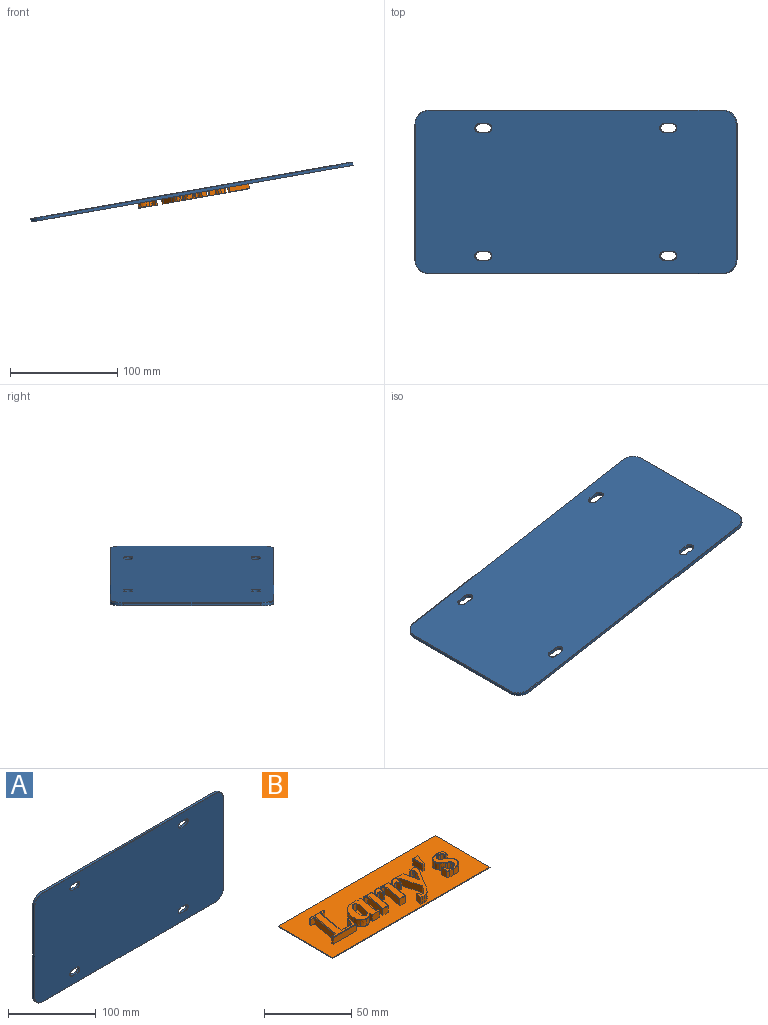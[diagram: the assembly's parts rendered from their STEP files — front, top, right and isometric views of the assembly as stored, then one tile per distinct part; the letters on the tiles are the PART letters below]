
ASSEMBLY  parts=2 mates=2
PART A: 50 faces, bbox 306.9x3.2x154.5 mm
  f0: cylinder r=12.7mm len=12.7mm, axis (0,1,0), area 55.7mm2, adj f1,f7,f9,f46
  f1: plane 279.4x2.79mm, normal (0,0,1), area 780.6mm2, adj f0,f2,f9,f44
  f2: cylinder r=12.7mm len=12.7mm, axis (0,1,0), area 55.7mm2, adj f1,f3,f9,f42
  f3: plane 127x2.79mm, normal (-1,0,0), area 354.8mm2, adj f2,f4,f9,f43
  f4: cylinder r=12.7mm len=12.7mm, axis (0,1,0), area 55.7mm2, adj f3,f5,f9,f45
  f5: plane 279.4x2.79mm, normal (0,0,-1), area 780.6mm2, adj f4,f6,f9,f47
  f6: cylinder r=12.7mm len=12.7mm, axis (0,1,0), area 55.7mm2, adj f5,f7,f9,f49
  f7: plane 127x2.79mm, normal (1,0,0), area 354.8mm2, adj f0,f6,f9,f48
  f8: plane 304.04x151.64mm, normal (0,-1,0), area 45497.2mm2, adj f26,f27,f28,f29,f30,f31,f32,f33
  f9: plane 304.8x152.4mm, normal (0,1,0), area 45898.4mm2, adj f0,f1,f2,f3,f4,f5,f6,f7
  f10: plane 7.62x2.79mm, normal (0,0,1), area 21.3mm2, adj f9,f11,f13,f39
  f11: cylinder r=3.81mm len=7.62mm, axis (0,-1,0), area 33.4mm2, adj f9,f10,f12,f41
  f12: plane 7.62x2.79mm, normal (0,0,-1), area 21.3mm2, adj f9,f11,f13,f40
  f13: cylinder r=3.81mm len=7.62mm, axis (0,-1,0), area 33.4mm2, adj f9,f10,f12,f38
  f14: cylinder r=3.81mm len=7.62mm, axis (0,-1,0), area 33.4mm2, adj f9,f15,f17,f34
  f15: plane 7.62x2.79mm, normal (0,0,1), area 21.3mm2, adj f9,f14,f16,f35
  f16: cylinder r=3.81mm len=7.62mm, axis (0,-1,0), area 33.4mm2, adj f9,f15,f17,f37
  f17: plane 7.62x2.79mm, normal (0,0,-1), area 21.3mm2, adj f9,f14,f16,f36
  f18: cylinder r=3.81mm len=7.62mm, axis (0,-1,0), area 33.4mm2, adj f9,f19,f21,f31
  f19: plane 7.62x2.79mm, normal (0,0,1), area 21.3mm2, adj f9,f18,f20,f33
  f20: cylinder r=3.81mm len=7.62mm, axis (0,-1,0), area 33.4mm2, adj f9,f19,f21,f32
  f21: plane 7.62x2.79mm, normal (0,0,-1), area 21.3mm2, adj f9,f18,f20,f30
  f22: cylinder r=3.81mm len=7.62mm, axis (0,-1,0), area 33.4mm2, adj f9,f23,f25,f27
  f23: plane 7.62x2.79mm, normal (0,0,1), area 21.3mm2, adj f9,f22,f24,f29
  f24: cylinder r=3.81mm len=7.62mm, axis (0,-1,0), area 33.4mm2, adj f9,f23,f25,f28
  f25: plane 7.62x2.79mm, normal (0,0,-1), area 21.3mm2, adj f9,f22,f24,f26
  f26: cylinder r=0.38mm len=7.62mm, axis (1,0,0), area 4.6mm2, adj f8,f25,f27,f28
  f27: torus R=4.19mm, axis (0,-1,0), area 7.4mm2, adj f8,f22,f26,f29
  f28: torus R=4.19mm, axis (0,-1,0), area 7.4mm2, adj f8,f24,f26,f29
  f29: cylinder r=0.38mm len=7.62mm, axis (-1,0,0), area 4.6mm2, adj f8,f23,f27,f28
  f30: cylinder r=0.38mm len=7.62mm, axis (1,0,0), area 4.6mm2, adj f8,f21,f31,f32
  f31: torus R=4.19mm, axis (0,-1,0), area 7.4mm2, adj f8,f18,f30,f33
  f32: torus R=4.19mm, axis (0,-1,0), area 7.4mm2, adj f8,f20,f30,f33
  f33: cylinder r=0.38mm len=7.62mm, axis (-1,0,0), area 4.6mm2, adj f8,f19,f31,f32
  f34: torus R=4.19mm, axis (0,-1,0), area 7.4mm2, adj f8,f14,f35,f36
  f35: cylinder r=0.38mm len=7.62mm, axis (-1,0,0), area 4.6mm2, adj f8,f15,f34,f37
  f36: cylinder r=0.38mm len=7.62mm, axis (1,0,0), area 4.6mm2, adj f8,f17,f34,f37
  f37: torus R=4.19mm, axis (0,-1,0), area 7.4mm2, adj f8,f16,f35,f36
  f38: torus R=4.19mm, axis (0,-1,0), area 7.4mm2, adj f8,f13,f39,f40
  f39: cylinder r=0.38mm len=7.62mm, axis (-1,0,0), area 4.6mm2, adj f8,f10,f38,f41
  f40: cylinder r=0.38mm len=7.62mm, axis (1,0,0), area 4.6mm2, adj f8,f12,f38,f41
  f41: torus R=4.19mm, axis (0,-1,0), area 7.4mm2, adj f8,f11,f39,f40
  f42: torus R=12.32mm, axis (0,-1,0), area 11.8mm2, adj f2,f8,f43,f44
  f43: cylinder r=0.38mm len=127mm, axis (0,0,1), area 76mm2, adj f3,f8,f42,f45
  f44: cylinder r=0.38mm len=279.4mm, axis (1,0,0), area 167.2mm2, adj f1,f8,f42,f46
  f45: torus R=12.32mm, axis (0,-1,0), area 11.8mm2, adj f4,f8,f43,f47
  f46: torus R=12.32mm, axis (0,-1,0), area 11.8mm2, adj f0,f8,f44,f48
  f47: cylinder r=0.38mm len=279.4mm, axis (-1,0,0), area 167.2mm2, adj f5,f8,f45,f49
  f48: cylinder r=0.38mm len=127mm, axis (0,0,-1), area 76mm2, adj f7,f8,f46,f49
  f49: torus R=12.32mm, axis (0,-1,0), area 11.8mm2, adj f6,f8,f47,f48
PART B: 223 faces, bbox 127x44.5x5.3 mm
  f0: plane 127x44.45mm, normal (0,0,1), area 4801.8mm2, adj f1,f2,f3,f4,f6,f7,f8,f9
  f1: plane 127x0.51mm, normal (0,-1,0), area 64.5mm2, adj f0,f2,f4,f5
  f2: plane 44.45x0.51mm, normal (1,0,0), area 22.6mm2, adj f0,f1,f3,f5
  f3: plane 127x0.51mm, normal (0,1,0), area 64.5mm2, adj f0,f2,f4,f5
  f4: plane 44.45x0.51mm, normal (-1,0,0), area 22.6mm2, adj f0,f1,f3,f5
  f5: plane 127x44.45mm, normal (0,0,-1), area 5645.2mm2, adj f1,f2,f3,f4
  f6: plane 19.57x4.46mm, normal (0.98,-0.17,0), area 88.6mm2, adj f0,f7,f21,f221
  f7: plane 4.46x3.48mm, normal (0.13,-0.99,0), area 15.6mm2, adj f0,f6,f8,f222
  f8: plane 4.46x1.26mm, normal (0.98,-0.18,0), area 5.7mm2, adj f0,f7,f9,f220
  f9: plane 11.42x4.46mm, normal (0,1,0), area 50.9mm2, adj f0,f8,f10,f218
  f10: plane 4.46x1.26mm, normal (-0.98,0.18,0), area 5.7mm2, adj f0,f9,f11,f216
  f11: plane 4.46x2.86mm, normal (-0.16,-0.99,0), area 12.9mm2, adj f0,f10,f12,f214
  f12: plane 19.67x4.46mm, normal (-0.98,0.17,0), area 89mm2, adj f0,f11,f13,f212
  f13: plane 4.46x3.05mm, normal (-0.15,0.99,0), area 13.7mm2, adj f0,f12,f14,f210
  f14: plane 4.46x1.26mm, normal (-0.99,0.16,0), area 5.7mm2, adj f0,f13,f15,f208
  f15: plane 18.69x4.46mm, normal (0,-1,0), area 83.3mm2, adj f0,f14,f16,f207
  f16: plane 6.98x4.46mm, normal (0.98,-0.21,0), area 31.8mm2, adj f0,f15,f17,f209
  f17: plane 4.46x1.45mm, normal (0,1,0), area 6.5mm2, adj f0,f16,f18,f211
  f18: plane 4.81x4.46mm, normal (-0.92,0.39,0), area 23.2mm2, adj f0,f17,f19,f213
  f19: extruded ~4.46x2.73mm, area 12.2mm2, adj f0,f18,f20,f215
  f20: extruded ~4.46x3.73mm, area 16.6mm2, adj f0,f19,f21,f217
  f21: plane 4.46x1.95mm, normal (0,1,0), area 8.7mm2, adj f0,f6,f20,f219
  f22: plane 22.49x19.49mm, normal (0,0,1), area 129.8mm2, adj f207,f208,f209,f210,f211,f212,f213,f214
  f23: plane 14.92x4.76mm, normal (0.98,-0.17,0), area 72.1mm2, adj f0,f24,f46,f47
  f24: plane 4.76x0.93mm, normal (0,1,0), area 4.4mm2, adj f0,f23,f25,f47
  f25: plane 4.76x1.41mm, normal (-0.41,0.91,0), area 7.4mm2, adj f0,f24,f26,f47
  f26: extruded ~4.76x4.32mm, area 21mm2, adj f0,f25,f27,f47
  f27: extruded ~4.96x4.76mm, area 25mm2, adj f0,f26,f28,f47
  f28: extruded ~4.76x4.05mm, area 25.8mm2, adj f0,f27,f29,f47
  f29: extruded ~5.59x4.76mm, area 27.5mm2, adj f0,f28,f30,f47
  f30: extruded ~4.76x4.31mm, area 21.7mm2, adj f0,f29,f31,f47
  f31: extruded ~4.76x3.35mm, area 18.3mm2, adj f0,f30,f32,f47
  f32: extruded ~4.76x2.61mm, area 13.1mm2, adj f0,f31,f33,f47
  f33: extruded ~4.76x2.3mm, area 14.6mm2, adj f0,f32,f34,f47
  f34: plane 4.76x2.38mm, normal (-1,-0.03,0), area 11.3mm2, adj f0,f33,f35,f47
  f35: plane 5.98x4.76mm, normal (0,-1,0), area 28.5mm2, adj f0,f34,f36,f47
  f36: plane 4.76x1mm, normal (0.99,-0.14,0), area 4.8mm2, adj f0,f35,f46,f47
  f37: extruded ~4.76x4.31mm, area 20.8mm2, adj f38,f45,f47,f48
  f38: extruded ~4.76x3.29mm, area 17.8mm2, adj f37,f39,f47,f48
  f39: extruded ~4.76x2.36mm, area 13mm2, adj f38,f40,f47,f48
  f40: extruded ~4.76x2.14mm, area 10.7mm2, adj f39,f41,f47,f48
  f41: plane 9.7x4.76mm, normal (-0.98,0.17,0), area 46.9mm2, adj f40,f42,f47,f48
  f42: extruded ~4.76x1.7mm, area 10.9mm2, adj f41,f43,f47,f48
  f43: extruded ~4.76x1.53mm, area 8.2mm2, adj f42,f44,f47,f48
  f44: extruded ~4.76x1.49mm, area 9.1mm2, adj f43,f45,f47,f48
  f45: extruded ~4.76x2.82mm, area 13.9mm2, adj f37,f44,f47,f48
  f46: plane 4.76x1.88mm, normal (0.28,0.96,0), area 9.3mm2, adj f0,f23,f36,f47
  f47: plane 16.97x16.38mm, normal (0,0,1), area 159.9mm2, adj f23,f24,f25,f26,f27,f28,f29,f30
  f48: plane 12.68x6.84mm, normal (0,0,1), area 60.8mm2, adj f37,f38,f39,f40,f41,f42,f43,f44
  f49: plane 4.46x3.48mm, normal (0.99,-0.11,0), area 15.6mm2, adj f0,f50,f63,f202
  f50: plane 6.46x4.46mm, normal (0,1,0), area 28.8mm2, adj f0,f49,f51,f200
  f51: plane 4.46x1.14mm, normal (-0.99,0.17,0), area 5.2mm2, adj f0,f50,f52,f198
  f52: plane 4.46x2.02mm, normal (-0.2,-0.98,0), area 9.2mm2, adj f0,f51,f53,f196
  f53: plane 14.64x4.46mm, normal (-0.98,0.17,0), area 66.3mm2, adj f0,f52,f54,f194
  f54: plane 4.64x4.46mm, normal (0,-1,0), area 20.7mm2, adj f0,f53,f55,f192
  f55: plane 10.27x4.46mm, normal (0.98,-0.17,0), area 46.5mm2, adj f0,f54,f56,f193
  f56: extruded ~4.46x2.08mm, area 12.5mm2, adj f0,f55,f57,f195
  f57: extruded ~4.46x2.25mm, area 10.6mm2, adj f0,f56,f58,f197
  f58: plane 4.46x2.36mm, normal (-0.95,-0.3,0), area 11mm2, adj f0,f57,f59,f199
  f59: plane 4.46x0.95mm, normal (0,-1,0), area 4.2mm2, adj f0,f58,f60,f201
  f60: plane 5.8x4.46mm, normal (0.99,-0.17,0), area 26.3mm2, adj f0,f59,f61,f203
  f61: extruded ~4.46x1.43mm, area 6.5mm2, adj f0,f60,f62,f205
  f62: extruded ~4.46x2.71mm, area 13.2mm2, adj f0,f61,f63,f206
  f63: extruded ~4.46x2.88mm, area 16.6mm2, adj f0,f49,f62,f204
  f64: plane 16.02x12.56mm, normal (0,0,1), area 79.7mm2, adj f192,f193,f194,f195,f196,f197,f198,f199
  f65: plane 4.46x3.48mm, normal (0.99,-0.11,0), area 15.6mm2, adj f0,f66,f79,f190
  f66: plane 6.46x4.46mm, normal (0,1,0), area 28.8mm2, adj f0,f65,f67,f191
  f67: plane 4.46x1.14mm, normal (-0.99,0.17,0), area 5.2mm2, adj f0,f66,f68,f189
  f68: plane 4.46x2.02mm, normal (-0.2,-0.98,0), area 9.2mm2, adj f0,f67,f69,f187
  f69: plane 14.64x4.46mm, normal (-0.98,0.17,0), area 66.3mm2, adj f0,f68,f70,f185
  f70: plane 4.64x4.46mm, normal (0,-1,0), area 20.7mm2, adj f0,f69,f71,f183
  f71: plane 10.27x4.46mm, normal (0.98,-0.17,0), area 46.5mm2, adj f0,f70,f72,f181
  f72: extruded ~4.46x2.08mm, area 12.5mm2, adj f0,f71,f73,f179
  f73: extruded ~4.46x2.25mm, area 10.6mm2, adj f0,f72,f74,f177
  f74: plane 4.46x2.36mm, normal (-0.95,-0.3,0), area 11mm2, adj f0,f73,f75,f178
  f75: plane 4.46x0.95mm, normal (0,-1,0), area 4.2mm2, adj f0,f74,f76,f180
  f76: plane 5.8x4.46mm, normal (0.99,-0.17,0), area 26.3mm2, adj f0,f75,f77,f182
  f77: extruded ~4.46x1.43mm, area 6.5mm2, adj f0,f76,f78,f184
  f78: extruded ~4.46x2.71mm, area 13.2mm2, adj f0,f77,f79,f186
  f79: extruded ~4.46x2.88mm, area 16.6mm2, adj f0,f65,f78,f188
  f80: plane 16.02x12.56mm, normal (0,0,1), area 79.7mm2, adj f177,f178,f179,f180,f181,f182,f183,f184
  f81: extruded ~4.76x1.09mm, area 5.8mm2, adj f0,f82,f107,f108
  f82: plane 4.76x3.98mm, normal (0,1,0), area 19mm2, adj f0,f81,f83,f108
  f83: plane 4.76x1.12mm, normal (-0.98,0.18,0), area 5.4mm2, adj f0,f82,f84,f108
  f84: extruded ~4.76x1.01mm, area 5.2mm2, adj f0,f83,f85,f108
  f85: extruded ~4.76x0.47mm, area 2.9mm2, adj f0,f84,f86,f108
  f86: extruded ~4.76x0.73mm, area 3.6mm2, adj f0,f85,f87,f108
  f87: extruded ~4.76x1.44mm, area 7mm2, adj f0,f86,f88,f108
  f88: extruded ~4.76x1.66mm, area 8.8mm2, adj f0,f87,f89,f108
  f89: plane 5.17x4.76mm, normal (-0.86,0.52,0), area 28.7mm2, adj f0,f88,f90,f108
  f90: plane 11.01x4.76mm, normal (0.97,0.23,0), area 53.9mm2, adj f0,f89,f91,f108
  f91: plane 5.21x4.76mm, normal (0,1,0), area 24.8mm2, adj f0,f90,f92,f108
  f92: plane 4.76x1.14mm, normal (-0.99,0.17,0), area 5.5mm2, adj f0,f91,f93,f108
  f93: plane 4.76x1.05mm, normal (-0.37,-0.93,0), area 5.4mm2, adj f0,f92,f94,f108
  f94: plane 14.73x4.76mm, normal (-0.97,-0.24,0), area 72.3mm2, adj f0,f93,f95,f108
  f95: extruded ~4.76x4.41mm, area 25.8mm2, adj f0,f94,f96,f108
  f96: extruded ~4.76x2.26mm, area 12.5mm2, adj f0,f95,f97,f108
  f97: extruded ~4.76x1.2mm, area 6.2mm2, adj f0,f96,f98,f108
  f98: plane 4.76x2.17mm, normal (0.99,0.16,0), area 10.4mm2, adj f0,f97,f99,f108
  f99: plane 4.76x1.03mm, normal (0,1,0), area 4.9mm2, adj f0,f98,f100,f108
  f100: plane 4.76x4.17mm, normal (-0.99,0.17,0), area 20.1mm2, adj f0,f99,f101,f108
  f101: extruded ~4.76x1.37mm, area 6.6mm2, adj f0,f100,f102,f108
  f102: extruded ~4.76x1.4mm, area 6.7mm2, adj f0,f101,f103,f108
  f103: extruded ~4.76x2.48mm, area 12.4mm2, adj f0,f102,f104,f108
  f104: extruded ~4.76x2.3mm, area 14.4mm2, adj f0,f103,f105,f108
  f105: extruded ~4.76x3.99mm, area 23.2mm2, adj f0,f104,f106,f108
  f106: plane 12.33x7.56mm, normal (0.85,-0.52,0), area 68.9mm2, adj f0,f105,f107,f108
  f107: extruded ~4.76x3.79mm, area 19.5mm2, adj f0,f81,f106,f108
  f108: plane 23.81x19.29mm, normal (0,0,1), area 132.3mm2, adj f81,f82,f83,f84,f85,f86,f87,f88
  f109: plane 8.28x4.46mm, normal (-1,0.02,0), area 36.9mm2, adj f0,f110,f112,f175
  f110: plane 4.46x1.45mm, normal (0,-1,0), area 6.5mm2, adj f0,f109,f111,f176
  f111: plane 8.28x4.46mm, normal (0.95,-0.32,0), area 39mm2, adj f0,f110,f112,f174
  f112: plane 4.46x4.1mm, normal (0,1,0), area 18.3mm2, adj f0,f109,f111,f173
  f113: plane 7.68x3.52mm, normal (0,0,1), area 16.5mm2, adj f173,f174,f175,f176
  f114: extruded ~4.38x1.91mm, area 8.6mm2, adj f0,f115,f142,f171
  f115: extruded ~4.38x1.47mm, area 8.1mm2, adj f0,f114,f116,f172
  f116: extruded ~4.38x2.35mm, area 12.4mm2, adj f0,f115,f117,f170
  f117: extruded ~4.38x2.23mm, area 12mm2, adj f0,f116,f118,f168
  f118: extruded ~4.38x1.26mm, area 6.1mm2, adj f0,f117,f119,f166
  f119: extruded ~4.38x1.53mm, area 7.4mm2, adj f0,f118,f120,f164
  f120: extruded ~4.38x1.92mm, area 9mm2, adj f0,f119,f121,f162
  f121: extruded ~4.38x1.59mm, area 7.2mm2, adj f0,f120,f122,f160
  f122: extruded ~4.38x1.07mm, area 5.9mm2, adj f0,f121,f123,f158
  f123: plane 4.38x1.89mm, normal (-0.99,-0.12,0), area 8.3mm2, adj f0,f122,f124,f156
  f124: plane 4.38x1.14mm, normal (0,-1,0), area 5mm2, adj f0,f123,f125,f154
  f125: plane 4.38x4.15mm, normal (0.98,-0.18,0), area 18.5mm2, adj f0,f124,f126,f152
  f126: extruded ~4.51x4.38mm, area 20mm2, adj f0,f125,f127,f150
  f127: extruded ~6.49x4.91mm, area 40.7mm2, adj f0,f126,f128,f148
  f128: extruded ~4.38x2.61mm, area 12.1mm2, adj f0,f127,f129,f146
  f129: extruded ~4.38x2.7mm, area 15.5mm2, adj f0,f128,f130,f144
  f130: plane 4.38x1.14mm, normal (-0.5,-0.87,0), area 5.8mm2, adj f0,f129,f131,f145
  f131: extruded ~4.38x1.42mm, area 7.9mm2, adj f0,f130,f132,f147
  f132: extruded ~4.38x1.23mm, area 5.9mm2, adj f0,f131,f133,f149
  f133: extruded ~4.38x1.87mm, area 9.3mm2, adj f0,f132,f134,f151
  f134: extruded ~4.38x2.25mm, area 10.7mm2, adj f0,f133,f135,f153
  f135: extruded ~4.38x3.05mm, area 15.6mm2, adj f0,f134,f136,f155
  f136: plane 4.38x2.28mm, normal (0.99,0.11,0), area 10mm2, adj f0,f135,f137,f157
  f137: plane 4.38x1.14mm, normal (0,1,0), area 5mm2, adj f0,f136,f138,f159
  f138: plane 4.5x4.38mm, normal (-0.98,0.17,0), area 20mm2, adj f0,f137,f139,f161
  f139: extruded ~4.38x2.26mm, area 10.3mm2, adj f0,f138,f140,f163
  f140: extruded ~4.38x2.85mm, area 12.6mm2, adj f0,f139,f141,f165
  f141: extruded ~5.25x4.38mm, area 24.3mm2, adj f0,f140,f142,f167
  f142: extruded ~4.38x4.04mm, area 20mm2, adj f0,f114,f141,f169
  f143: plane 16.21x11.96mm, normal (0,0,1), area 76.2mm2, adj f144,f145,f146,f147,f148,f149,f150,f151
  f144: bspline ~3.92x3.27mm, area 2.1mm2, adj f129,f143,f145,f146
  f145: cylinder r=0.38mm len=1.33mm, axis (-0.87,0.5,0), area 0.8mm2, adj f130,f143,f144,f147
  f146: bspline ~3.56x1.4mm, area 1.6mm2, adj f128,f143,f144,f148
  f147: bspline ~2.31x1.95mm, area 1.1mm2, adj f131,f143,f145,f149
  f148: bspline ~7.48x7.14mm, area 5.4mm2, adj f127,f143,f146,f150
  f149: bspline ~1.91x0.99mm, area 0.9mm2, adj f132,f143,f147,f151
  f150: bspline ~5.64x0.98mm, area 2.6mm2, adj f126,f143,f148,f152
  f151: bspline ~3.21x1.7mm, area 1.3mm2, adj f133,f143,f149,f153
  f152: cylinder r=0.38mm len=4.22mm, axis (-0.18,-0.98,0), area 2.3mm2, adj f125,f143,f150,f154
  f153: bspline ~3.78x1.44mm, area 1.5mm2, adj f134,f143,f151,f155
  f154: cylinder r=0.38mm len=1.14mm, axis (-1,0,0), area 0.5mm2, adj f124,f143,f152,f156
  f155: bspline ~6.09x4.05mm, area 2.2mm2, adj f135,f143,f153,f157
  f156: cylinder r=0.38mm len=2.04mm, axis (-0.12,0.99,0), area 1.1mm2, adj f123,f143,f154,f158
  f157: cylinder r=0.38mm len=2.42mm, axis (0.11,-0.99,0), area 1.3mm2, adj f136,f143,f155,f159
  f158: bspline ~1.8x1.64mm, area 0.9mm2, adj f122,f143,f156,f160
  f159: cylinder r=0.38mm len=1.14mm, axis (1,0,0), area 0.5mm2, adj f137,f143,f157,f161
  f160: bspline ~2.38x0.9mm, area 1mm2, adj f121,f143,f158,f162
  f161: cylinder r=0.38mm len=4.56mm, axis (0.17,0.98,0), area 2.5mm2, adj f138,f143,f159,f163
  f162: bspline ~3.2x1.23mm, area 1.3mm2, adj f120,f143,f160,f164
  f163: bspline ~3.48x1.35mm, area 1.3mm2, adj f139,f143,f161,f165
  f164: bspline ~2.29x1.37mm, area 1.1mm2, adj f119,f143,f162,f166
  f165: bspline ~3.91x0.78mm, area 1.7mm2, adj f140,f143,f163,f167
  f166: bspline ~1.84x0.96mm, area 0.9mm2, adj f118,f143,f164,f168
  f167: bspline ~7.42x2.49mm, area 3.3mm2, adj f141,f143,f165,f169
  f168: bspline ~3.34x2.48mm, area 1.7mm2, adj f117,f143,f166,f170
  f169: bspline ~6.36x3.1mm, area 2.7mm2, adj f142,f143,f167,f171
  f170: bspline ~3.57x2.6mm, area 1.7mm2, adj f116,f143,f168,f172
  f171: bspline ~2.67x0.91mm, area 1.1mm2, adj f114,f143,f169,f172
  f172: bspline ~2.02x1.58mm, area 1.1mm2, adj f115,f143,f170,f171
  f173: cylinder r=0.3mm len=4.1mm, axis (1,0,0), area 1.8mm2, adj f112,f113,f174,f175
  f174: cylinder r=0.3mm len=8.38mm, axis (-0.32,-0.95,0), area 4mm2, adj f111,f113,f173,f176
  f175: cylinder r=0.3mm len=8.29mm, axis (0.02,1,0), area 3.8mm2, adj f109,f113,f173,f176
  f176: cylinder r=0.3mm len=1.45mm, axis (-1,0,0), area 0.6mm2, adj f110,f113,f174,f175
  f177: bspline ~4.86x1.28mm, area 1.2mm2, adj f73,f80,f178,f179
  f178: cylinder r=0.3mm len=2.66mm, axis (-0.3,0.95,0), area 1.2mm2, adj f74,f80,f177,f180
  f179: bspline ~3x2.89mm, area 1.4mm2, adj f72,f80,f177,f181
  f180: cylinder r=0.3mm len=0.95mm, axis (-1,0,0), area 0.3mm2, adj f75,f80,f178,f182
  f181: cylinder r=0.3mm len=10.38mm, axis (-0.17,-0.98,0), area 4.9mm2, adj f71,f80,f179,f183
  f182: cylinder r=0.3mm len=5.86mm, axis (-0.17,-0.99,0), area 2.7mm2, adj f76,f80,f180,f184
  f183: cylinder r=0.3mm len=4.64mm, axis (-1,0,0), area 2.1mm2, adj f70,f80,f181,f185
  f184: bspline ~1.96x0.54mm, area 0.6mm2, adj f77,f80,f182,f186
  f185: cylinder r=0.3mm len=14.99mm, axis (0.17,0.98,0), area 7.1mm2, adj f69,f80,f183,f187
  f186: bspline ~3.44x1.37mm, area 1.4mm2, adj f78,f80,f184,f188
  f187: cylinder r=0.3mm len=2.37mm, axis (-0.98,0.2,0), area 1mm2, adj f68,f80,f185,f189
  f188: bspline ~6.77x4.84mm, area 2.2mm2, adj f79,f80,f186,f190
  f189: cylinder r=0.3mm len=1.19mm, axis (0.17,0.99,0), area 0.4mm2, adj f67,f80,f187,f191
  f190: cylinder r=0.3mm len=5.18mm, axis (-0.11,-0.99,0), area 2mm2, adj f65,f80,f188,f191
  f191: cylinder r=0.3mm len=6.46mm, axis (1,0,0), area 2.9mm2, adj f66,f80,f189,f190
  f192: cylinder r=0.3mm len=4.64mm, axis (-1,0,0), area 2.1mm2, adj f54,f64,f193,f194
  f193: cylinder r=0.3mm len=10.38mm, axis (-0.17,-0.98,0), area 4.9mm2, adj f55,f64,f192,f195
  f194: cylinder r=0.3mm len=14.99mm, axis (0.17,0.98,0), area 7.1mm2, adj f53,f64,f192,f196
  f195: bspline ~3x2.89mm, area 1.4mm2, adj f56,f64,f193,f197
  f196: cylinder r=0.3mm len=2.37mm, axis (-0.98,0.2,0), area 1mm2, adj f52,f64,f194,f198
  f197: bspline ~4.86x1.28mm, area 1.2mm2, adj f57,f64,f195,f199
  f198: cylinder r=0.3mm len=1.19mm, axis (0.17,0.99,0), area 0.4mm2, adj f51,f64,f196,f200
  f199: cylinder r=0.3mm len=2.66mm, axis (-0.3,0.95,0), area 1.2mm2, adj f58,f64,f197,f201
  f200: cylinder r=0.3mm len=6.46mm, axis (1,0,0), area 2.9mm2, adj f50,f64,f198,f202
  f201: cylinder r=0.3mm len=0.95mm, axis (-1,0,0), area 0.3mm2, adj f59,f64,f199,f203
  f202: cylinder r=0.3mm len=5.18mm, axis (-0.11,-0.99,0), area 2mm2, adj f49,f64,f200,f204
  f203: cylinder r=0.3mm len=5.86mm, axis (-0.17,-0.99,0), area 2.7mm2, adj f60,f64,f201,f205
  f204: bspline ~6.77x4.84mm, area 2.2mm2, adj f63,f64,f202,f206
  f205: bspline ~1.96x0.54mm, area 0.6mm2, adj f61,f64,f203,f206
  f206: bspline ~3.44x1.37mm, area 1.4mm2, adj f62,f64,f204,f205
  f207: cylinder r=0.3mm len=18.69mm, axis (-1,0,0), area 8.8mm2, adj f15,f22,f208,f209
  f208: cylinder r=0.3mm len=1.31mm, axis (0.16,0.99,0), area 0.5mm2, adj f14,f22,f207,f210
  f209: cylinder r=0.3mm len=7.04mm, axis (-0.21,-0.98,0), area 3.3mm2, adj f16,f22,f207,f211
  f210: cylinder r=0.3mm len=3.31mm, axis (0.99,0.15,0), area 1.5mm2, adj f13,f22,f208,f212
  f211: cylinder r=0.3mm len=1.45mm, axis (1,0,0), area 0.6mm2, adj f17,f22,f209,f213
  f212: cylinder r=0.3mm len=20.24mm, axis (0.17,0.98,0), area 9.7mm2, adj f12,f22,f210,f214
  f213: cylinder r=0.3mm len=5.08mm, axis (0.39,0.92,0), area 2.5mm2, adj f18,f22,f211,f215
  f214: cylinder r=0.3mm len=3.21mm, axis (-0.99,0.16,0), area 1.4mm2, adj f11,f22,f212,f216
  f215: bspline ~4.19x0.71mm, area 1.4mm2, adj f19,f22,f213,f217
  f216: cylinder r=0.3mm len=1.31mm, axis (0.18,0.98,0), area 0.5mm2, adj f10,f22,f214,f218
  f217: bspline ~5.14x0.46mm, area 1.8mm2, adj f20,f22,f215,f219
  f218: cylinder r=0.3mm len=11.42mm, axis (1,0,0), area 5.3mm2, adj f9,f22,f216,f220
  f219: cylinder r=0.3mm len=2.31mm, axis (1,0,0), area 1mm2, adj f21,f22,f217,f221
  f220: cylinder r=0.3mm len=1.31mm, axis (-0.18,-0.98,0), area 0.5mm2, adj f8,f22,f218,f222
  f221: cylinder r=0.3mm len=20.2mm, axis (-0.17,-0.98,0), area 9.7mm2, adj f6,f22,f219,f222
  f222: cylinder r=0.3mm len=3.74mm, axis (-0.99,-0.13,0), area 1.7mm2, adj f7,f22,f220,f221
PLACE A rot(axis=(-0.99,-0.09,-0.09),90.4deg) t=(-132.68,201.01,200.53)mm
PLACE B rot(axis=(0,1,0),170deg) t=(-133.11,254.99,200.97)mm
MATE planar A.f1 <-> B.f3  axis (0,1,0) through (-132.93,277.21,201.9)mm
MATE planar A.f9 <-> B.f0  axis (0.17,0,-0.98) through (-132.68,201.01,200.53)mm
